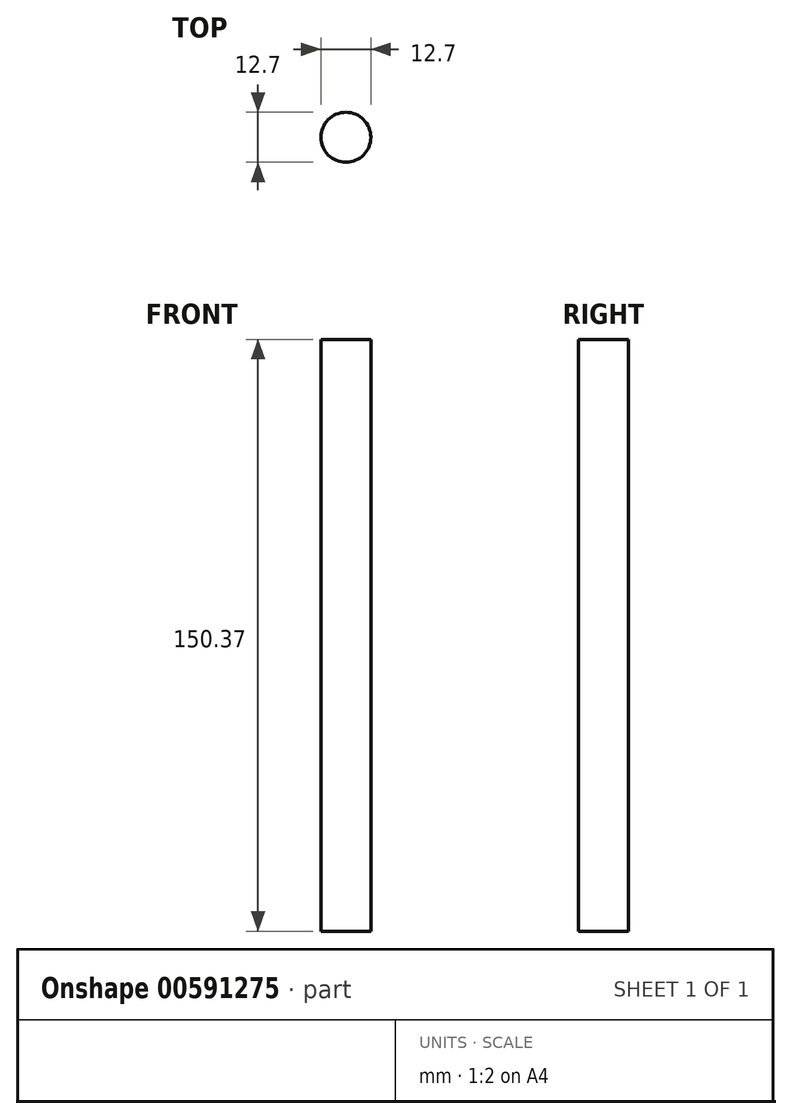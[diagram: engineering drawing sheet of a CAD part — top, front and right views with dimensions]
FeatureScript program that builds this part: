
annotation { "Feature Type Name" : "Feature", "Feature Type Description" : "" }
export const myFeature = defineFeature(function(context is Context, id is Id, definition is map)
    precondition{}
    {
        {
            var Q0;
            Q0=qCreatedBy(makeId("Top.planeOp"),FACE);
            var sketch = newSketch(context, id + "F0", { "sketchPlane" : qUnion([Q0])});
            skCircle(sketch, "E0", {"center": v(0, 0) * mm, "radius": 6.35 * mm});
            skSolve(sketch);
        }
        {
            var Q0;
            Q0 = qSketchRegion(id + "F0", true);
            extrude(context, id + "F1", {"entities" : qUnion([Q0]), "depth" : 150.37 * mm, "offsetDistance" : 25.4 * mm});
        }
    });
